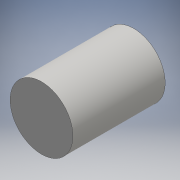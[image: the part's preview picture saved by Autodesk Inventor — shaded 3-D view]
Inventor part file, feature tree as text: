
AUTODESK INVENTOR PART (.ipt)
format: ipt  version: 2016 (Build 200138000, 138)  size: 111,104 bytes
history: native  units: mm
features: hole x4, extrude x2, sketch x2, other x1
ambient origin geometry x8: Origin, YZ Plane, XZ Plane, XY Plane, X Axis, Y Axis, Z Axis, Center Point
bodies: Body1 (feature_tree)
feature tree (9):
  other  "ソリッド1"
  extrude  "押し出し1"  Depth=40.0mm
  extrude  "押し出し2"  Depth=58.7mm TaperAngle=0.0deg
  hole  "穴1"  [1 undecoded]
  hole  "穴2"  [1 undecoded]
  hole  "穴3"  [1 undecoded]
  hole  "穴4"  [1 undecoded]
  sketch  "スケッチ1"
  sketch  "スケッチ2"
note: 4 required parameter values undecoded (feature->parameter linkage not recoverable at this tier; creation-order binding heuristic only, values carry confidence <= 0.55)
